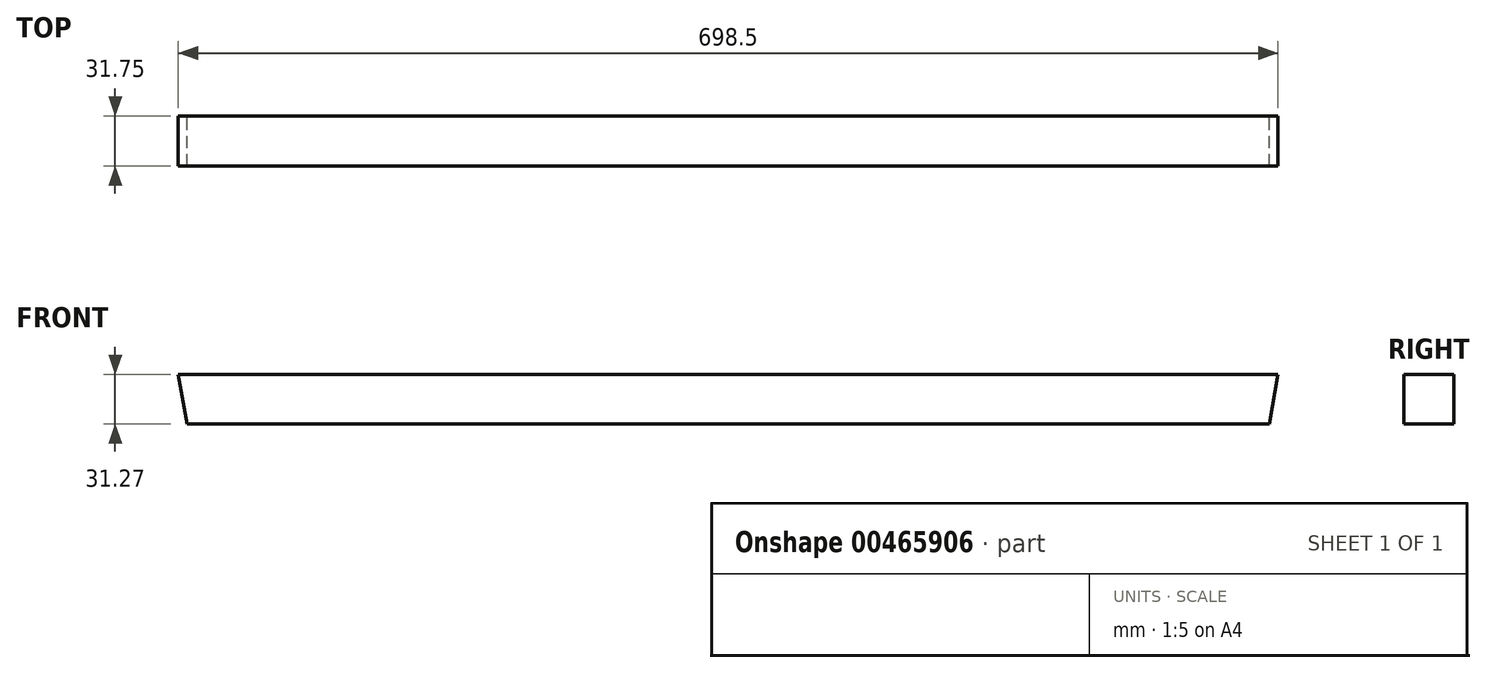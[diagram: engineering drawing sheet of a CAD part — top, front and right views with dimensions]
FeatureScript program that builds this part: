
annotation { "Feature Type Name" : "Feature", "Feature Type Description" : "" }
export const myFeature = defineFeature(function(context is Context, id is Id, definition is map)
    precondition{}
    {
        {
            var Q0;
            Q0=qCreatedBy(makeId("Front.planeOp"),FACE);
            var sketch = newSketch(context, id + "F0", { "sketchPlane" : qUnion([Q0])});
            skLineSegment(sketch, "E0", {"start": v(-104.54, 31.27) * mm, "end": v(593.96, 31.27) * mm});
            skLineSegment(sketch, "E1", {"start": v(593.96, 31.27) * mm, "end": v(588.44, 0) * mm});
            skLineSegment(sketch, "E2", {"start": v(-104.54, 31.27) * mm, "end": v(-99.03, 0) * mm});
            skLineSegment(sketch, "E3", {"start": v(-99.03, 0) * mm, "end": v(588.44, 0) * mm});
            skSolve(sketch);
        }
        {
            var Q0;
            Q0=makeQuery(id+"F0.imprint","IMPRINT",FACE,{"disambiguationData":[TD([[makeQuery(id+"F0.imprint","IMPRINT",EDGE,{"derivedFrom":sQuery(id+"F0.wireOp",EDGE,"E0")}),-1.0]])]});
            extrude(context, id + "F1", {"entities" : qUnion([Q0]), "depth" : 31.75 * mm});
        }
    });
